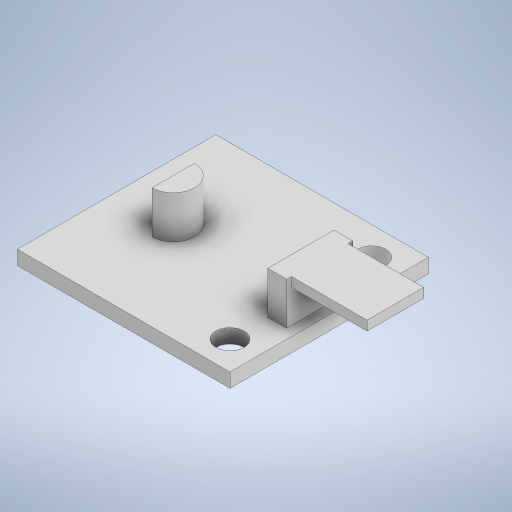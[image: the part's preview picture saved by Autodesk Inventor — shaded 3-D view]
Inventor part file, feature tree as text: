
AUTODESK INVENTOR PART (.ipt)
format: ipt  version: 2024 (Build 280153000, 153)  size: 267,776 bytes
history: native  units: mm
features: extrude x3, sketch x3
ambient origin geometry x8: Origin, YZ Plane, XZ Plane, XY Plane, X Axis, Y Axis, Z Axis, Center Point
bodies: Solid1 (feature_tree)
feature tree (6):
  extrude  "Extrusion1"  Depth=22.5mm
  extrude  "Extrusion2"  Depth=3.0mm
  extrude  "Extrusion3"  Depth=1.5mm TaperAngle=0.0deg
  sketch  "Sketch1"  dims[d0=21.0mm d1=22.5mm]
  sketch  "Sketch2"  dims[d2=3.0mm d5=3.0mm]
  sketch  "Sketch3"  dims[d8=3.0mm d9=1.5mm d10=0.0mm d11=4.5mm d12=7.0mm d13=2.0mm d14=1.0mm d15=6.0mm d16=4.5mm d17=0.0mm d18=6.0mm d19=1.0mm d21=0.5mm d22=0.5mm d23=8.0mm d24=0.0mm d25=15.0mm d26=3.0mm]
